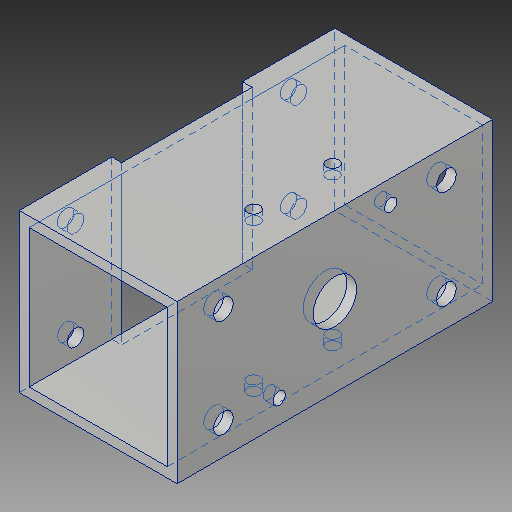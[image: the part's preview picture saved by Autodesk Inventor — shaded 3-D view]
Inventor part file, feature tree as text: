
AUTODESK INVENTOR PART (.ipt)
format: ipt  version: 2019 (Build 230136000, 136)  size: 170,496 bytes
history: native  units: in
note: dims shown in document units (in); Inventor stores cm internally (conversion verified against a paired STEP export)
features: reference x11, extrude x6, sketch x6, other x5
ambient origin geometry x8: Origin, YZ Plane, XZ Plane, XY Plane, X Axis, Y Axis, Z Axis, Center Point
bodies: Solid1 (feature_tree)
feature tree (28):
  extrude  "Extrusion1"  Depth=0.125in
  extrude  "Extrusion7"  Depth=2.0in
  extrude  "Extrusion8"  Depth=1.654in
  extrude  "Extrusion9"  Depth=0.125in TaperAngle=0.0deg
  extrude  "Extrusion10"  Depth=0.125in TaperAngle=0.0deg
  extrude  "Extrusion11"  Depth=1.0in TaperAngle=0.0deg
  sketch  "Sketch1"  dims[d0=2.0in d1=0.125in]
  sketch  "Sketch6"  dims[d2=4.0in d3=0.0in d11=2.0in]
  sketch  "Sketch7"  dims[d12=0.125in d23=1.654in]
  reference  "Reference2"
  reference  "Reference3"
  sketch  "Sketch8"  dims[d24=0.125in d25=0.0in d26=0.125in d27=0.0in]
  reference  "Reference4"
  sketch  "Sketch9"  dims[d28=0.55in d29=0.125in d30=0.0in]
  reference  "Reference5"
  reference  "Reference6"
  reference  "Reference7"
  reference  "Reference8"
  sketch  "Sketch10"  dims[d31=0.21in d32=1.0in d33=0.0in d34=1.0in d35=0.0in]
  reference  "Reference9"
  reference  "Reference10"
  reference  "Reference11"
  reference  "Reference12"
  parser-record x1  (decoder bookkeeping rows leaked as tree rows — omitted from the tree; the rows remain in map.json)
  other  "Drive Arm.iam"
  other  "Gearbox:1"
  other  "217-2625-026 Rev1_1"
  other  "Arm 18 inch:1"
note: 1 file-system path scrubbed to <path> (originals preserved in map.json)
